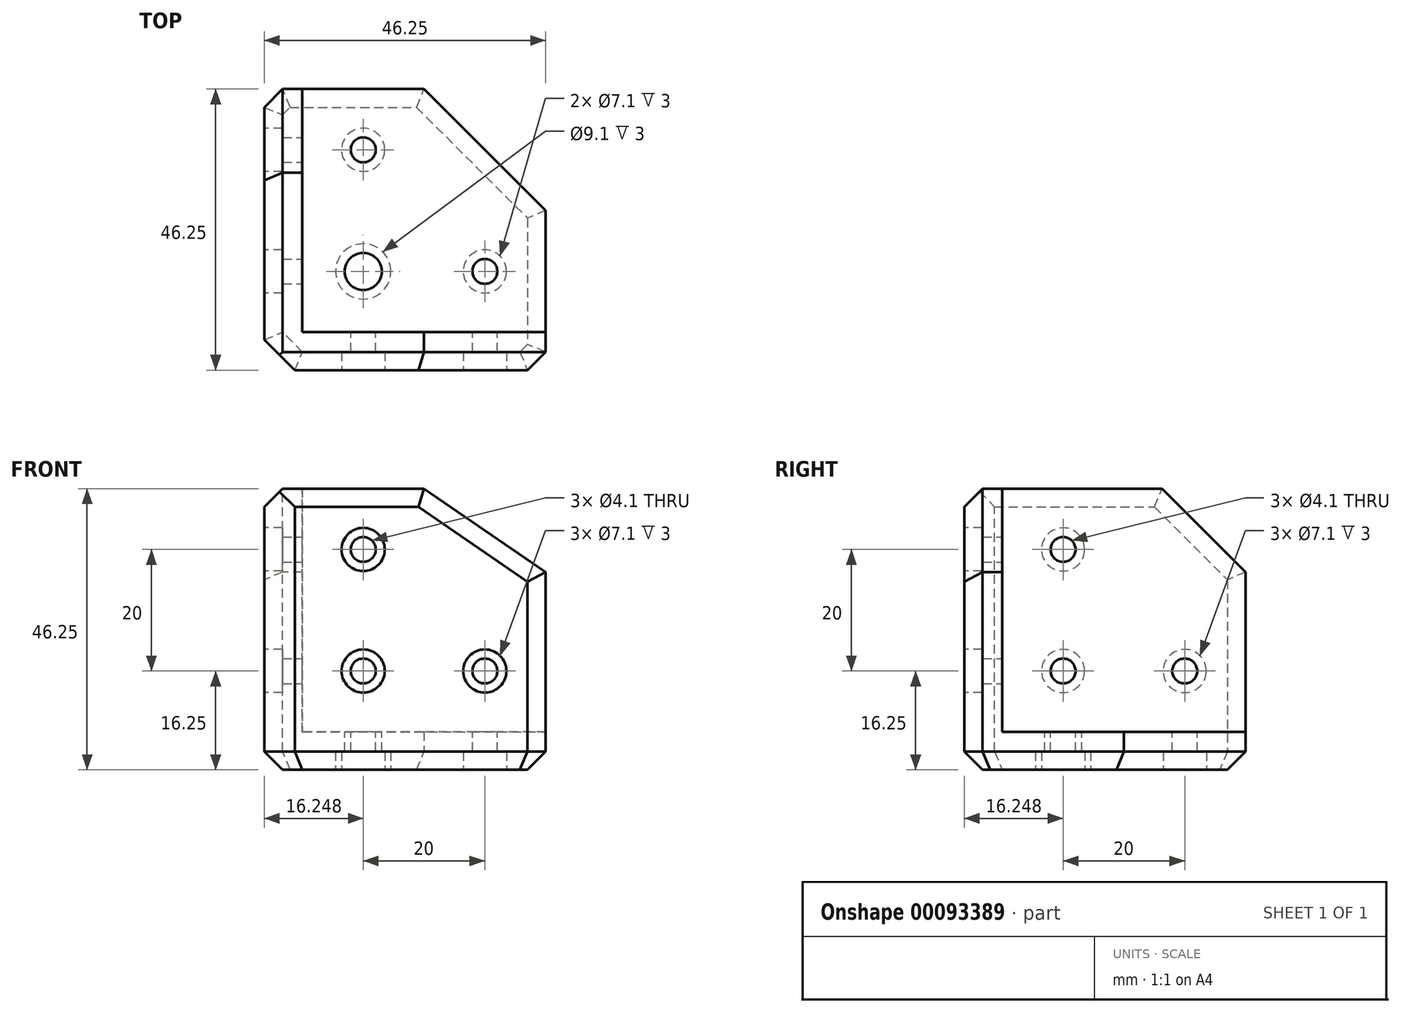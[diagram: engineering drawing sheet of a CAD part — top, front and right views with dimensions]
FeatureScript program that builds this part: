
annotation { "Feature Type Name" : "Feature", "Feature Type Description" : "" }
export const myFeature = defineFeature(function(context is Context, id is Id, definition is map)
    precondition{}
    {
        {
            var Q0;
            Q0=qCreatedBy(makeId("Top.planeOp"),FACE);
            var sketch = newSketch(context, id + "F0", { "sketchPlane" : qUnion([Q0])});
            skLineSegment(sketch, "E0", {"start": v(-22.1, 32.56) * mm, "end": v(-22.1, -13.7) * mm});
            skLineSegment(sketch, "E1", {"start": v(-22.1, -13.7) * mm, "end": v(24.15, -13.7) * mm});
            skLineSegment(sketch, "E2", {"start": v(24.15, -13.7) * mm, "end": v(24.15, 12.56) * mm});
            skLineSegment(sketch, "E3", {"start": v(24.15, 12.56) * mm, "end": v(4.15, 32.56) * mm});
            skLineSegment(sketch, "E4", {"start": v(4.15, 32.56) * mm, "end": v(-22.1, 32.56) * mm});
            skLineSegment(sketch, "E5", {"start": v(-15.85, 32.56) * mm, "end": v(-15.85, -7.44) * mm, "construction": true});
            skLineSegment(sketch, "E6", {"start": v(-15.85, -7.44) * mm, "end": v(24.15, -7.44) * mm, "construction": true});
            skSolve(sketch);
        }
        {
            var Q0;
            Q0=qSketchRegion(id+"F0",true);
            extrude(context, id + "F1", {"entities" : qUnion([Q0]), "depth" : 6.25 * mm});
        }
        {
            var Q0;
            Q0=makeQuery(id+"F1.opExtrude","SWEPT_FACE",FACE,{"disambiguationData":[OSD([sQuery(id+"F0.wireOp",EDGE,"E1")])]});
            var sketch = newSketch(context, id + "F2", { "sketchPlane" : qUnion([Q0])});
            skLineSegment(sketch, "E7", {"start": v(-22.1, 6.25) * mm, "end": v(24.15, 6.25) * mm});
            skLineSegment(sketch, "E8", {"start": v(24.15, 6.25) * mm, "end": v(24.15, 32.5) * mm});
            skLineSegment(sketch, "E9", {"start": v(24.15, 32.5) * mm, "end": v(4.15, 46.25) * mm});
            skLineSegment(sketch, "E10", {"start": v(-22.1, 6.25) * mm, "end": v(-22.1, 46.25) * mm});
            skLineSegment(sketch, "E11", {"start": v(-22.1, 46.25) * mm, "end": v(4.15, 46.25) * mm});
            skSolve(sketch);
        }
        {
            var Q0;
            Q0=qSketchRegion(id+"F2",true);
            extrude(context, id + "F3", {"entities" : qUnion([Q0]), "oppositeDirection" : true, "depth" : 6.25 * mm});
        }
        {
            var Q0;
            Q0=makeQuery(id+"F3.opExtrude","SWEPT_FACE",FACE,{"disambiguationData":[OSD([sQuery(id+"F2.wireOp",EDGE,"E10")])]});
            var sketch = newSketch(context, id + "F4", { "sketchPlane" : qUnion([Q0])});
            skLineSegment(sketch, "E12", {"start": v(7.44, 6.25) * mm, "end": v(-32.56, 6.25) * mm});
            skLineSegment(sketch, "E13", {"start": v(7.44, 6.25) * mm, "end": v(7.44, 46.25) * mm});
            skLineSegment(sketch, "E14", {"start": v(7.44, 46.25) * mm, "end": v(-18.8, 46.25) * mm});
            skLineSegment(sketch, "E15", {"start": v(-18.8, 46.25) * mm, "end": v(-32.56, 32.5) * mm});
            skLineSegment(sketch, "E16", {"start": v(-32.56, 32.5) * mm, "end": v(-32.56, 6.25) * mm});
            skSolve(sketch);
        }
        {
            var Q0;
            Q0=qSketchRegion(id+"F4",true);
            extrude(context, id + "F5", {"entities" : qUnion([Q0]), "oppositeDirection" : true, "depth" : 6.25 * mm});
        }
        {
            var Q0;
            Q0=makeQuery(id+"F1.opExtrude","CAP_FACE",FACE,{"disambiguationData":[OSD([sQuery(id+"F0.wireOp",EDGE,"E0"),sQuery(id+"F0.wireOp",EDGE,"E1"),sQuery(id+"F0.wireOp",EDGE,"E2"),sQuery(id+"F0.wireOp",EDGE,"E3"),sQuery(id+"F0.wireOp",EDGE,"E4")])],"isStart":false});
            var sketch = newSketch(context, id + "F6", { "sketchPlane" : qUnion([Q0])});
            skCircle(sketch, "E17", {"center": v(-5.85, 22.56) * mm, "radius": 2.05 * mm});
            skCircle(sketch, "E18", {"center": v(-5.85, 2.56) * mm, "radius": 3.05 * mm});
            skCircle(sketch, "E19", {"center": v(14.15, 2.56) * mm, "radius": 2.05 * mm});
            skSolve(sketch);
        }
        {
            var Q0;
            Q0=qSketchRegion(id+"F6",true);
            extrude(context, id + "F7", {"entities" : qUnion([Q0]), "operationType" : NewBodyOperationType.REMOVE, "oppositeDirection" : true, "depth" : 25 * mm});
        }
        {
            var Q0;
            Q0=makeQuery(id+"F3.opExtrude","CAP_FACE",FACE,{"disambiguationData":[OSD([sQuery(id+"F2.wireOp",EDGE,"E7"),sQuery(id+"F2.wireOp",EDGE,"E8"),sQuery(id+"F2.wireOp",EDGE,"E9"),sQuery(id+"F2.wireOp",EDGE,"E10"),sQuery(id+"F2.wireOp",EDGE,"E11")])],"isStart":false});
            var sketch = newSketch(context, id + "F8", { "sketchPlane" : qUnion([Q0])});
            skCircle(sketch, "E20", {"center": v(5.85, 16.25) * mm, "radius": 2.05 * mm});
            skCircle(sketch, "E21", {"center": v(-14.15, 16.25) * mm, "radius": 2.05 * mm});
            skCircle(sketch, "E22", {"center": v(5.85, 36.25) * mm, "radius": 2.05 * mm});
            skSolve(sketch);
        }
        {
            var Q0;
            Q0=qSketchRegion(id+"F8",true);
            extrude(context, id + "F9", {"entities" : qUnion([Q0]), "operationType" : NewBodyOperationType.REMOVE, "oppositeDirection" : true, "depth" : 25 * mm});
        }
        {
            var Q0;
            Q0=makeQuery(id+"F5.opExtrude","CAP_FACE",FACE,{"disambiguationData":[OSD([sQuery(id+"F4.wireOp",EDGE,"E12"),sQuery(id+"F4.wireOp",EDGE,"E13"),sQuery(id+"F4.wireOp",EDGE,"E14"),sQuery(id+"F4.wireOp",EDGE,"E15"),sQuery(id+"F4.wireOp",EDGE,"E16")])],"isStart":false});
            var sketch = newSketch(context, id + "F10", { "sketchPlane" : qUnion([Q0])});
            skCircle(sketch, "E23", {"center": v(22.56, 16.25) * mm, "radius": 2.05 * mm});
            skCircle(sketch, "E24", {"center": v(2.56, 16.25) * mm, "radius": 2.05 * mm});
            skCircle(sketch, "E25", {"center": v(2.56, 36.25) * mm, "radius": 2.05 * mm});
            skSolve(sketch);
        }
        {
            var Q0;
            Q0=qSketchRegion(id+"F10",true);
            extrude(context, id + "F11", {"entities" : qUnion([Q0]), "operationType" : NewBodyOperationType.REMOVE, "oppositeDirection" : true, "depth" : 25 * mm});
        }
        {
            var Q0;
            Q0=makeQuery(id+"F1.opExtrude","SWEPT_BODY",BODY,{"disambiguationData":[OSD([sQuery(id+"F0.wireOp",EDGE,"E0"),sQuery(id+"F0.wireOp",EDGE,"E1"),sQuery(id+"F0.wireOp",EDGE,"E2"),sQuery(id+"F0.wireOp",EDGE,"E3"),sQuery(id+"F0.wireOp",EDGE,"E4")])]});
            var Q1;
            Q1=makeQuery(id+"F3.opExtrude","SWEPT_BODY",BODY,{"disambiguationData":[OSD([sQuery(id+"F2.wireOp",EDGE,"E7"),sQuery(id+"F2.wireOp",EDGE,"E8"),sQuery(id+"F2.wireOp",EDGE,"E9"),sQuery(id+"F2.wireOp",EDGE,"E10"),sQuery(id+"F2.wireOp",EDGE,"E11")])]});
            var Q2;
            Q2=makeQuery(id+"F5.opExtrude","SWEPT_BODY",BODY,{"disambiguationData":[OSD([sQuery(id+"F4.wireOp",EDGE,"E12"),sQuery(id+"F4.wireOp",EDGE,"E13"),sQuery(id+"F4.wireOp",EDGE,"E14"),sQuery(id+"F4.wireOp",EDGE,"E15"),sQuery(id+"F4.wireOp",EDGE,"E16")])]});
            booleanBodies(context, id + "F12", {"operationType" : BooleanOperationType.UNION, "tools" : qUnion([Q0, Q1, Q2])});
        }
        {
            var Q0;
            Q0=makeQuery(id+"F12.opBoolean","MERGE",FACE,{"derivedFrom":[makeQuery(id+"F1.opExtrude","SWEPT_FACE",FACE,{"disambiguationData":[OSD([sQuery(id+"F0.wireOp",EDGE,"E1")])]}),makeQuery(id+"F3.opExtrude","CAP_FACE",FACE,{"disambiguationData":[OSD([sQuery(id+"F2.wireOp",EDGE,"E7"),sQuery(id+"F2.wireOp",EDGE,"E8"),sQuery(id+"F2.wireOp",EDGE,"E9"),sQuery(id+"F2.wireOp",EDGE,"E10"),sQuery(id+"F2.wireOp",EDGE,"E11")])],"isStart":true})]});
            var sketch = newSketch(context, id + "F13", { "sketchPlane" : qUnion([Q0])});
            skCircle(sketch, "E26", {"center": v(-5.85, 36.25) * mm, "radius": 3.55 * mm});
            skCircle(sketch, "E27", {"center": v(14.15, 16.25) * mm, "radius": 3.55 * mm});
            skCircle(sketch, "E28", {"center": v(-5.85, 16.25) * mm, "radius": 3.55 * mm});
            skSolve(sketch);
        }
        {
            var Q0;
            Q0=qSketchRegion(id+"F13",true);
            extrude(context, id + "F14", {"entities" : qUnion([Q0]), "operationType" : NewBodyOperationType.REMOVE, "oppositeDirection" : true, "depth" : 3 * mm});
        }
        {
            var Q0;
            Q0=makeQuery(id+"F12.opBoolean","MERGE",FACE,{"derivedFrom":[makeQuery(id+"F1.opExtrude","SWEPT_FACE",FACE,{"disambiguationData":[OSD([sQuery(id+"F0.wireOp",EDGE,"E0")])]}),makeQuery(id+"F3.opExtrude","SWEPT_FACE",FACE,{"disambiguationData":[OSD([sQuery(id+"F2.wireOp",EDGE,"E10")])]}),makeQuery(id+"F5.opExtrude","CAP_FACE",FACE,{"disambiguationData":[OSD([sQuery(id+"F4.wireOp",EDGE,"E12"),sQuery(id+"F4.wireOp",EDGE,"E13"),sQuery(id+"F4.wireOp",EDGE,"E14"),sQuery(id+"F4.wireOp",EDGE,"E15"),sQuery(id+"F4.wireOp",EDGE,"E16")])],"isStart":true})]});
            var sketch = newSketch(context, id + "F15", { "sketchPlane" : qUnion([Q0])});
            skCircle(sketch, "E29", {"center": v(-2.56, 36.25) * mm, "radius": 3.55 * mm});
            skCircle(sketch, "E30", {"center": v(-2.56, 16.25) * mm, "radius": 3.55 * mm});
            skCircle(sketch, "E31", {"center": v(-22.56, 16.25) * mm, "radius": 3.55 * mm});
            skSolve(sketch);
        }
        {
            var Q0;
            Q0=qSketchRegion(id+"F15",true);
            extrude(context, id + "F16", {"entities" : qUnion([Q0]), "operationType" : NewBodyOperationType.REMOVE, "oppositeDirection" : true, "depth" : 3 * mm});
        }
        {
            var Q0;
            Q0=makeQuery(id+"F1.opExtrude","CAP_FACE",FACE,{"disambiguationData":[OSD([sQuery(id+"F0.wireOp",EDGE,"E0"),sQuery(id+"F0.wireOp",EDGE,"E1"),sQuery(id+"F0.wireOp",EDGE,"E2"),sQuery(id+"F0.wireOp",EDGE,"E3"),sQuery(id+"F0.wireOp",EDGE,"E4")])],"isStart":true});
            var sketch = newSketch(context, id + "F17", { "sketchPlane" : qUnion([Q0])});
            skCircle(sketch, "E32", {"center": v(-5.85, -22.56) * mm, "radius": 3.55 * mm});
            skCircle(sketch, "E33", {"center": v(-5.85, -2.56) * mm, "radius": 4.55 * mm});
            skCircle(sketch, "E34", {"center": v(14.15, -2.56) * mm, "radius": 3.55 * mm});
            skSolve(sketch);
        }
        {
            var Q0;
            Q0=qSketchRegion(id+"F17",true);
            extrude(context, id + "F18", {"entities" : qUnion([Q0]), "operationType" : NewBodyOperationType.REMOVE, "oppositeDirection" : true, "depth" : 3 * mm});
        }
        {
            var Q0;
            Q0=makeQuery(id+"F12.opBoolean","MERGE",EDGE,{"derivedFrom":[makeQuery(id+"F1.opExtrude","SWEPT_EDGE",EDGE,{"disambiguationData":[OSD([sQuery(id+"F0.wireOp",EDGE,"E0"),sQuery(id+"F0.wireOp",EDGE,"E1")])]}),makeQuery(id+"F3.opExtrude","CAP_EDGE",EDGE,{"disambiguationData":[OSD([sQuery(id+"F2.wireOp",EDGE,"E10")])],"isStart":true})]});
            chamfer(context, id + "F19", {"entities" : qUnion([Q0]), "width" : 5 * mm, "tangentPropagation" : true});
        }
        {
            var Q0;
            Q0=makeQuery(id+"F3.opExtrude","CAP_EDGE",EDGE,{"disambiguationData":[OSD([sQuery(id+"F2.wireOp",EDGE,"E11")])],"isStart":true});
            var Q1;
            Q1=makeQuery(id+"F12.opBoolean","MERGE",EDGE,{"derivedFrom":[makeQuery(id+"F3.opExtrude","SWEPT_EDGE",EDGE,{"disambiguationData":[OSD([sQuery(id+"F2.wireOp",EDGE,"E10"),sQuery(id+"F2.wireOp",EDGE,"E11")])]}),makeQuery(id+"F5.opExtrude","CAP_EDGE",EDGE,{"disambiguationData":[OSD([sQuery(id+"F4.wireOp",EDGE,"E14")])],"isStart":true})]});
            var Q2;
            Q2=makeQuery(id+"F3.opExtrude","CAP_EDGE",EDGE,{"disambiguationData":[OSD([sQuery(id+"F2.wireOp",EDGE,"E9")])],"isStart":true});
            var Q3;
            Q3=makeQuery(id+"F5.opExtrude","CAP_EDGE",EDGE,{"disambiguationData":[OSD([sQuery(id+"F4.wireOp",EDGE,"E15")])],"isStart":true});
            var Q4;
            Q4=makeQuery(id+"F12.opBoolean","MERGE",EDGE,{"derivedFrom":[makeQuery(id+"F1.opExtrude","SWEPT_EDGE",EDGE,{"disambiguationData":[OSD([sQuery(id+"F0.wireOp",EDGE,"E1"),sQuery(id+"F0.wireOp",EDGE,"E2")])]}),makeQuery(id+"F3.opExtrude","CAP_EDGE",EDGE,{"disambiguationData":[OSD([sQuery(id+"F2.wireOp",EDGE,"E8")])],"isStart":true})]});
            var Q5;
            Q5=makeQuery(id+"F12.opBoolean","MERGE",EDGE,{"derivedFrom":[makeQuery(id+"F1.opExtrude","SWEPT_EDGE",EDGE,{"disambiguationData":[OSD([sQuery(id+"F0.wireOp",EDGE,"E0"),sQuery(id+"F0.wireOp",EDGE,"E4")])]}),makeQuery(id+"F5.opExtrude","CAP_EDGE",EDGE,{"disambiguationData":[OSD([sQuery(id+"F4.wireOp",EDGE,"E16")])],"isStart":true})]});
            chamfer(context, id + "F20", {"entities" : qUnion([Q0, Q1, Q2, Q3, Q4, Q5]), "width" : 3 * mm, "tangentPropagation" : true});
        }
        {
            var Q0;
            {var subQ0=sQuery(id+"F0.wireOp",EDGE,"E2");var subQ1=sQuery(id+"F0.wireOp",EDGE,"E1");Q0=makeQuery(id+"F20.opChamfer","BLEND_EDGE",EDGE,{"blendedFrom":[makeQuery(id+"F12.opBoolean","MERGE",EDGE,{"derivedFrom":[makeQuery(id+"F1.opExtrude","SWEPT_EDGE",EDGE,{"disambiguationData":[OSD([subQ1,subQ0])]}),makeQuery(id+"F3.opExtrude","CAP_EDGE",EDGE,{"disambiguationData":[OSD([sQuery(id+"F2.wireOp",EDGE,"E8")])],"isStart":true})]}),makeQuery(id+"F1.opExtrude","CAP_FACE",FACE,{"disambiguationData":[OSD([sQuery(id+"F0.wireOp",EDGE,"E0"),subQ1,subQ0,sQuery(id+"F0.wireOp",EDGE,"E3"),sQuery(id+"F0.wireOp",EDGE,"E4")])],"isStart":true})],"blendedInto":[makeQuery(id+"F1.opExtrude","CAP_FACE",FACE,{"disambiguationData":[OSD([sQuery(id+"F0.wireOp",EDGE,"E0"),subQ1,subQ0,sQuery(id+"F0.wireOp",EDGE,"E3"),sQuery(id+"F0.wireOp",EDGE,"E4")])],"isStart":true})]});}
            var Q1;
            Q1=makeQuery(id+"F1.opExtrude","CAP_EDGE",EDGE,{"disambiguationData":[OSD([sQuery(id+"F0.wireOp",EDGE,"E2")])],"isStart":true});
            var Q2;
            Q2=makeQuery(id+"F1.opExtrude","CAP_EDGE",EDGE,{"disambiguationData":[OSD([sQuery(id+"F0.wireOp",EDGE,"E3")])],"isStart":true});
            var Q3;
            Q3=makeQuery(id+"F1.opExtrude","CAP_EDGE",EDGE,{"disambiguationData":[OSD([sQuery(id+"F0.wireOp",EDGE,"E4")])],"isStart":true});
            var Q4;
            {var subQ0=sQuery(id+"F0.wireOp",EDGE,"E4");var subQ1=sQuery(id+"F0.wireOp",EDGE,"E0");Q4=makeQuery(id+"F20.opChamfer","BLEND_EDGE",EDGE,{"blendedFrom":[makeQuery(id+"F12.opBoolean","MERGE",EDGE,{"derivedFrom":[makeQuery(id+"F1.opExtrude","SWEPT_EDGE",EDGE,{"disambiguationData":[OSD([subQ1,subQ0])]}),makeQuery(id+"F5.opExtrude","CAP_EDGE",EDGE,{"disambiguationData":[OSD([sQuery(id+"F4.wireOp",EDGE,"E16")])],"isStart":true})]}),makeQuery(id+"F1.opExtrude","CAP_FACE",FACE,{"disambiguationData":[OSD([subQ1,sQuery(id+"F0.wireOp",EDGE,"E1"),sQuery(id+"F0.wireOp",EDGE,"E2"),sQuery(id+"F0.wireOp",EDGE,"E3"),subQ0])],"isStart":true})],"blendedInto":[makeQuery(id+"F1.opExtrude","CAP_FACE",FACE,{"disambiguationData":[OSD([subQ1,sQuery(id+"F0.wireOp",EDGE,"E1"),sQuery(id+"F0.wireOp",EDGE,"E2"),sQuery(id+"F0.wireOp",EDGE,"E3"),subQ0])],"isStart":true})]});}
            var Q5;
            Q5=makeQuery(id+"F1.opExtrude","CAP_EDGE",EDGE,{"disambiguationData":[OSD([sQuery(id+"F0.wireOp",EDGE,"E0")])],"isStart":true});
            var Q6;
            {var subQ0=sQuery(id+"F0.wireOp",EDGE,"E1");var subQ1=sQuery(id+"F0.wireOp",EDGE,"E0");Q6=makeQuery(id+"F19.opChamfer","BLEND_EDGE",EDGE,{"blendedFrom":[makeQuery(id+"F12.opBoolean","MERGE",EDGE,{"derivedFrom":[makeQuery(id+"F1.opExtrude","SWEPT_EDGE",EDGE,{"disambiguationData":[OSD([subQ1,subQ0])]}),makeQuery(id+"F3.opExtrude","CAP_EDGE",EDGE,{"disambiguationData":[OSD([sQuery(id+"F2.wireOp",EDGE,"E10")])],"isStart":true})]}),makeQuery(id+"F1.opExtrude","CAP_FACE",FACE,{"disambiguationData":[OSD([subQ1,subQ0,sQuery(id+"F0.wireOp",EDGE,"E2"),sQuery(id+"F0.wireOp",EDGE,"E3"),sQuery(id+"F0.wireOp",EDGE,"E4")])],"isStart":true})],"blendedInto":[makeQuery(id+"F1.opExtrude","CAP_FACE",FACE,{"disambiguationData":[OSD([subQ1,subQ0,sQuery(id+"F0.wireOp",EDGE,"E2"),sQuery(id+"F0.wireOp",EDGE,"E3"),sQuery(id+"F0.wireOp",EDGE,"E4")])],"isStart":true})]});}
            var Q7;
            Q7=makeQuery(id+"F1.opExtrude","CAP_EDGE",EDGE,{"disambiguationData":[OSD([sQuery(id+"F0.wireOp",EDGE,"E1")])],"isStart":true});
            chamfer(context, id + "F21", {"entities" : qUnion([Q0, Q1, Q2, Q3, Q4, Q5, Q6, Q7]), "width" : 3 * mm, "tangentPropagation" : true});
        }
    });
